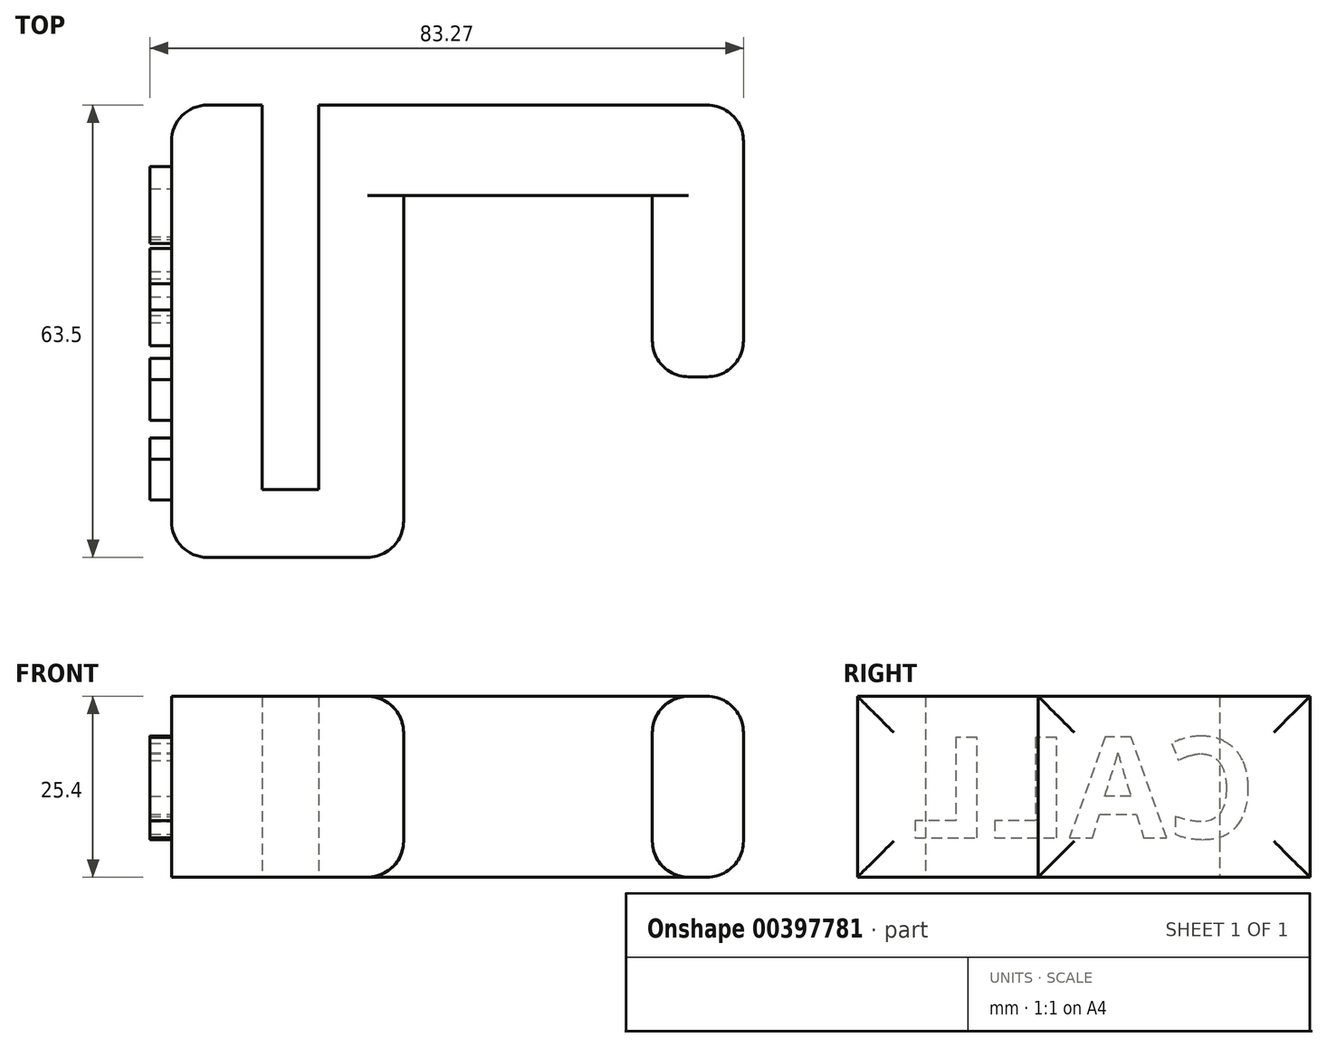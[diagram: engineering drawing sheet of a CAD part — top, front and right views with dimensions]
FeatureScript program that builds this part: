
annotation { "Feature Type Name" : "Feature", "Feature Type Description" : "" }
export const myFeature = defineFeature(function(context is Context, id is Id, definition is map)
    precondition{}
    {
        {
            var Q0;
            Q0=qCreatedBy(makeId("Top.planeOp"),FACE);
            var sketch = newSketch(context, id + "F0", { "sketchPlane" : qUnion([Q0])});
            skLineSegment(sketch, "E0", {"start": v(0, 0) * mm, "end": v(0, 63.5) * mm});
            skLineSegment(sketch, "E1", {"start": v(0, 63.5) * mm, "end": v(12.7, 63.5) * mm});
            skLineSegment(sketch, "E2", {"start": v(12.7, 63.5) * mm, "end": v(12.7, 9.53) * mm});
            skLineSegment(sketch, "E3", {"start": v(12.7, 9.53) * mm, "end": v(20.64, 9.53) * mm});
            skLineSegment(sketch, "E4", {"start": v(20.64, 9.53) * mm, "end": v(20.64, 63.5) * mm});
            skLineSegment(sketch, "E5", {"start": v(20.64, 63.5) * mm, "end": v(80.27, 63.5) * mm});
            skLineSegment(sketch, "E6", {"start": v(80.27, 63.5) * mm, "end": v(80.27, 25.35) * mm});
            skLineSegment(sketch, "E7", {"start": v(80.27, 25.35) * mm, "end": v(67.48, 25.35) * mm});
            skLineSegment(sketch, "E8", {"start": v(67.48, 25.35) * mm, "end": v(67.48, 50.8) * mm});
            skLineSegment(sketch, "E9", {"start": v(67.48, 50.8) * mm, "end": v(32.58, 50.8) * mm});
            skLineSegment(sketch, "E10", {"start": v(32.58, 50.8) * mm, "end": v(32.58, 0) * mm});
            skLineSegment(sketch, "E11", {"start": v(32.58, 0) * mm, "end": v(0, 0) * mm});
            skSolve(sketch);
        }
        {
            var Q0;
            Q0=makeQuery(id+"F0.imprint","IMPRINT",FACE,{"disambiguationData":[TD([[makeQuery(id+"F0.imprint","IMPRINT",EDGE,{"derivedFrom":sQuery(id+"F0.wireOp",EDGE,"E0")}),-1.0]])]});
            extrude(context, id + "F1", {"entities" : qUnion([Q0]), "depth" : 25.4 * mm});
        }
        {
            var Q0;
            Q0=makeQuery(id+"F1.opExtrude","SWEPT_EDGE",EDGE,{"disambiguationData":[OSD([sQuery(id+"F0.wireOp",EDGE,"E5"),sQuery(id+"F0.wireOp",EDGE,"E6")])]});
            var Q1;
            Q1=makeQuery(id+"F1.opExtrude","SWEPT_EDGE",EDGE,{"disambiguationData":[OSD([sQuery(id+"F0.wireOp",EDGE,"E6"),sQuery(id+"F0.wireOp",EDGE,"E7")])]});
            var Q2;
            Q2=makeQuery(id+"F1.opExtrude","SWEPT_EDGE",EDGE,{"disambiguationData":[OSD([sQuery(id+"F0.wireOp",EDGE,"E7"),sQuery(id+"F0.wireOp",EDGE,"E8")])]});
            var Q3;
            Q3=makeQuery(id+"F1.opExtrude","SWEPT_EDGE",EDGE,{"disambiguationData":[OSD([sQuery(id+"F0.wireOp",EDGE,"E10"),sQuery(id+"F0.wireOp",EDGE,"E11")])]});
            var Q4;
            Q4=makeQuery(id+"F1.opExtrude","SWEPT_EDGE",EDGE,{"disambiguationData":[OSD([sQuery(id+"F0.wireOp",EDGE,"E0"),sQuery(id+"F0.wireOp",EDGE,"E11")])]});
            var Q5;
            Q5=makeQuery(id+"F1.opExtrude","SWEPT_EDGE",EDGE,{"disambiguationData":[OSD([sQuery(id+"F0.wireOp",EDGE,"E0"),sQuery(id+"F0.wireOp",EDGE,"E1")])]});
            var Q6;
            Q6=makeQuery(id+"F1.opExtrude","CAP_EDGE",EDGE,{"disambiguationData":[OSD([sQuery(id+"F0.wireOp",EDGE,"E10")])],"isStart":false});
            var Q7;
            Q7=makeQuery(id+"F1.opExtrude","CAP_EDGE",EDGE,{"disambiguationData":[OSD([sQuery(id+"F0.wireOp",EDGE,"E8")])],"isStart":false});
            var Q8;
            Q8=makeQuery(id+"F1.opExtrude","CAP_EDGE",EDGE,{"disambiguationData":[OSD([sQuery(id+"F0.wireOp",EDGE,"E6")])],"isStart":false});
            var Q9;
            Q9=makeQuery(id+"F1.opExtrude","CAP_EDGE",EDGE,{"disambiguationData":[OSD([sQuery(id+"F0.wireOp",EDGE,"E6")])],"isStart":true});
            var Q10;
            Q10=makeQuery(id+"F1.opExtrude","CAP_EDGE",EDGE,{"disambiguationData":[OSD([sQuery(id+"F0.wireOp",EDGE,"E8")])],"isStart":true});
            var Q11;
            Q11=makeQuery(id+"F1.opExtrude","CAP_EDGE",EDGE,{"disambiguationData":[OSD([sQuery(id+"F0.wireOp",EDGE,"E10")])],"isStart":true});
            fillet(context, id + "F2", {"entities" : qUnion([Q0, Q1, Q2, Q3, Q4, Q5, Q6, Q7, Q8, Q9, Q10, Q11]), "radius" : 5.08 * mm, "tangentPropagation" : true, "allowEdgeOverflow" : false});
        }
        {
            var Q0;
            Q0=makeQuery(id+"F1.opExtrude","SWEPT_FACE",FACE,{"disambiguationData":[OSD([sQuery(id+"F0.wireOp",EDGE,"E0")])]});
            var sketch = newSketch(context, id + "F3", { "sketchPlane" : qUnion([Q0])});
            skText(sketch, "E12", { "text": "CALL", "fontName": "OpenSans-Bold.ttf"});
            const initialGuessF3  = {"E12": [-0.05599, 0.0055, 1, 0, 0.01424]};
            skSetInitialGuess(sketch, initialGuessF3);
            skSolve(sketch);
        }
        {
            var Q0;
            Q0 = qSketchRegion(id + "F3", true);
            extrude(context, id + "F4", {"entities" : qUnion([Q0]), "operationType" : NewBodyOperationType.ADD, "depth" : 3 * mm});
        }
    });
